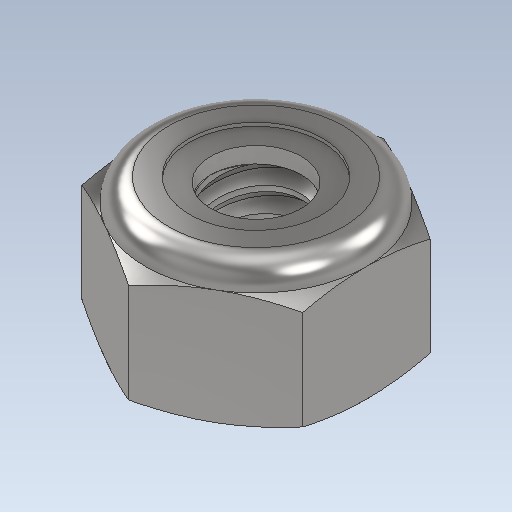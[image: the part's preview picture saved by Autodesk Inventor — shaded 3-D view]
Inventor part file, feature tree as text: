
AUTODESK INVENTOR PART (.ipt)
format: ipt  version: 2023 (Build 270158000, 158)  size: 310,784 bytes
history: native  units: in
note: dims shown in document units (in); Inventor stores cm internally (conversion verified against a paired STEP export)
features: other x1, revolve x1
ambient origin geometry x8: Origin, YZ Plane, XZ Plane, XY Plane, X Axis, Y Axis, Z Axis, Center Point
bodies: Solid1 (feature_tree), Solid2 (feature_tree)
feature tree (2):
  other  "Cut-Revolve4"
  revolve  "Revolve2"  [1 undecoded]
note: 1 required parameter value undecoded (feature->parameter linkage not recoverable at this tier; creation-order binding heuristic only, values carry confidence <= 0.55)
